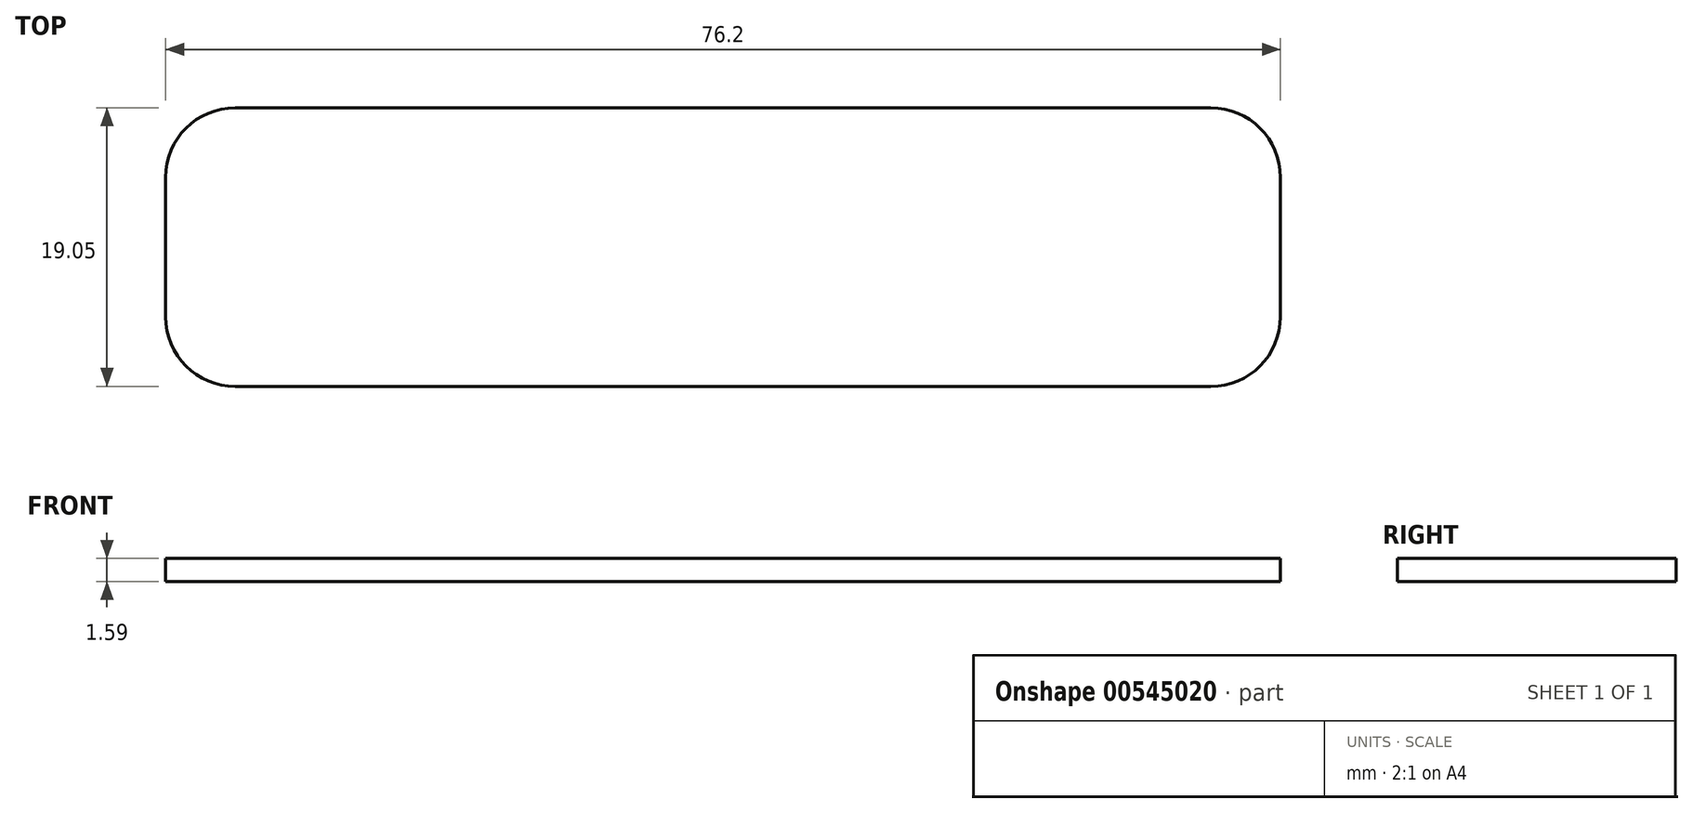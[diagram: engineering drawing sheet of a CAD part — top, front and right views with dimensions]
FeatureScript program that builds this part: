
annotation { "Feature Type Name" : "Feature", "Feature Type Description" : "" }
export const myFeature = defineFeature(function(context is Context, id is Id, definition is map)
    precondition{}
    {
        {
            var Q0;
            Q0=qCreatedBy(makeId("Top.planeOp"),FACE);
            var sketch = newSketch(context, id + "F0", { "sketchPlane" : qUnion([Q0])});
            skLineSegment(sketch, "E0.bottom", {"start": v(4.76, 0) * mm, "end": v(71.44, 0) * mm});
            skLineSegment(sketch, "E0.top", {"start": v(4.76, 19.05) * mm, "end": v(71.44, 19.05) * mm});
            skLineSegment(sketch, "E0.left", {"start": v(0, 4.76) * mm, "end": v(0, 14.29) * mm});
            skLineSegment(sketch, "E0.right", {"start": v(76.2, 4.76) * mm, "end": v(76.2, 14.29) * mm});
            skPoint(sketch, "E1.visualSharp", {"position": v(76.2, 19.05) * mm});
            skArc(sketch, "E1.filletArc", {"start": v(76.2, 14.29) * mm, "mid": v(74.8, 17.66) * mm, "end": v(71.44, 19.05) * mm});
            skPoint(sketch, "E2.visualSharp", {"position": v(76.2, 0) * mm});
            skArc(sketch, "E2.filletArc", {"start": v(71.44, 0) * mm, "mid": v(74.8, 1.4) * mm, "end": v(76.2, 4.76) * mm});
            skPoint(sketch, "E3.visualSharp", {"position": v(0, 0) * mm});
            skArc(sketch, "E3.filletArc", {"start": v(0, 4.76) * mm, "mid": v(1.4, 1.4) * mm, "end": v(4.76, 0) * mm});
            skPoint(sketch, "E4.visualSharp", {"position": v(0, 19.05) * mm});
            skArc(sketch, "E4.filletArc", {"start": v(4.76, 19.05) * mm, "mid": v(1.4, 17.66) * mm, "end": v(0, 14.29) * mm});
            skSolve(sketch);
        }
        {
            var Q0;
            Q0 = qSketchRegion(id + "F0", true);
            extrude(context, id + "F1", {"entities" : qUnion([Q0]), "depth" : 1.59 * mm, "offsetDistance" : 25.4 * mm});
        }
    });
